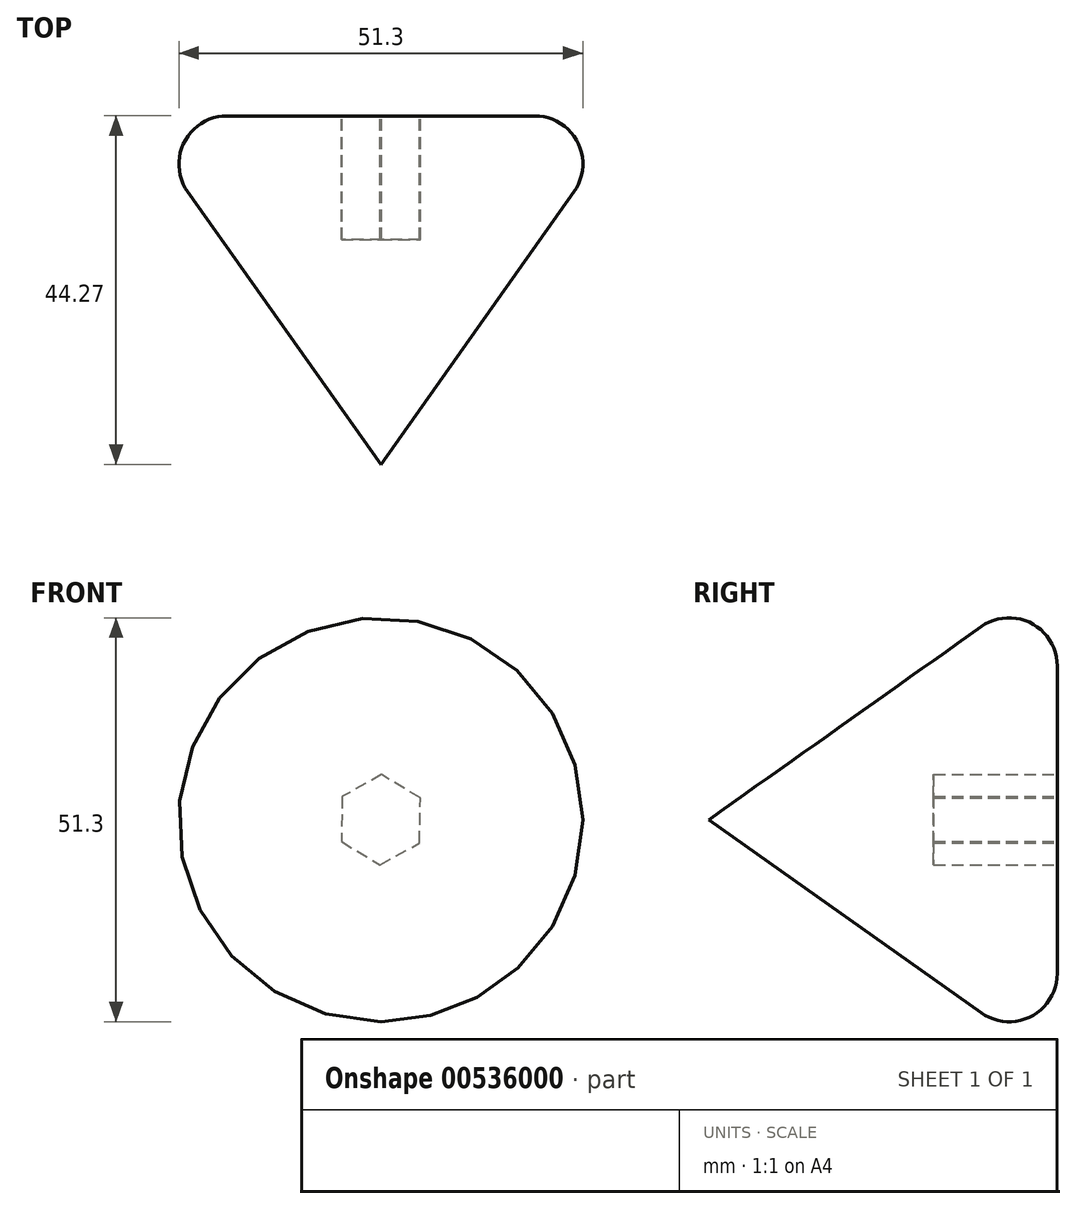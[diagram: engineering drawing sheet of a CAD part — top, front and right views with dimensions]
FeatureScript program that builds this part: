
annotation { "Feature Type Name" : "Feature", "Feature Type Description" : "" }
export const myFeature = defineFeature(function(context is Context, id is Id, definition is map)
    precondition{}
    {
        {
            var Q0;
            Q0=qCreatedBy(makeId("Top.planeOp"),FACE);
            var sketch = newSketch(context, id + "F0", { "sketchPlane" : qUnion([Q0])});
            skLineSegment(sketch, "E0", {"start": v(0, 18.72) * mm, "end": v(-31.37, 18.72) * mm});
            skLineSegment(sketch, "E1", {"start": v(-31.37, 18.72) * mm, "end": v(0, -25.55) * mm});
            skLineSegment(sketch, "E2", {"start": v(0, -25.55) * mm, "end": v(0, 18.72) * mm});
            skSolve(sketch);
        }
        {
            var Q0;
            Q0=makeQuery(id+"F0.imprint","IMPRINT",FACE,{"disambiguationData":[TD([[makeQuery(id+"F0.imprint","IMPRINT",EDGE,{"derivedFrom":sQuery(id+"F0.wireOp",EDGE,"E0")}),1.0]])]});
            var Q1;
            Q1=sQuery(id+"F0.wireOp",EDGE,"E2");
            revolve(context, id + "F1", {"entities" : qUnion([Q0]), "axis" : qUnion([Q1]), "revolveType" : RevolveType.FULL});
        }
        {
            var Q0;
            Q0=makeQuery(id+"F1.opRevolve","SWEPT_EDGE",EDGE,{"disambiguationData":[OSD([sQuery(id+"F0.wireOp",EDGE,"E0"),sQuery(id+"F0.wireOp",EDGE,"E1")])]});
            fillet(context, id + "F2", {"entities" : qUnion([Q0]), "radius" : 6.12 * mm, "tangentPropagation" : true, "allowEdgeOverflow" : false});
        }
        {
            var Q0;
            Q0=makeQuery(id+"F1.opRevolve","SWEPT_FACE",FACE,{"disambiguationData":[OSD([sQuery(id+"F0.wireOp",EDGE,"E0")])]});
            var sketch = newSketch(context, id + "F3", { "sketchPlane" : qUnion([Q0])});
            skCircle(sketch, "E3.cCircle", {"center": v(0, 0) * mm, "radius": 4.96 * mm, "construction": true});
            skLineSegment(sketch, "E3.0", {"start": v(-5, 2.78) * mm, "end": v(-0.1, 5.73) * mm});
            skLineSegment(sketch, "E3.1", {"start": v(-0.1, 5.73) * mm, "end": v(4.91, 2.95) * mm});
            skLineSegment(sketch, "E3.2", {"start": v(4.91, 2.95) * mm, "end": v(5, -2.78) * mm});
            skLineSegment(sketch, "E3.3", {"start": v(5, -2.78) * mm, "end": v(0.1, -5.73) * mm});
            skLineSegment(sketch, "E3.4", {"start": v(0.1, -5.73) * mm, "end": v(-4.91, -2.95) * mm});
            skLineSegment(sketch, "E3.5", {"start": v(-4.91, -2.95) * mm, "end": v(-5, 2.78) * mm});
            skPoint(sketch, "E3.0.midPoint", {"position": v(-2.55, 4.25) * mm});
            skSolve(sketch);
        }
        {
            var Q0;
            Q0=makeQuery(id+"F3.imprint","IMPRINT",FACE,{"disambiguationData":[TD([[makeQuery(id+"F3.imprint","IMPRINT",EDGE,{"derivedFrom":sQuery(id+"F3.wireOp",EDGE,"E3.0")}),-1.0]])]});
            extrude(context, id + "F4", {"entities" : qUnion([Q0]), "operationType" : NewBodyOperationType.REMOVE, "oppositeDirection" : true, "depth" : 15.7 * mm, "offsetDistance" : 25 * mm});
        }
    });
